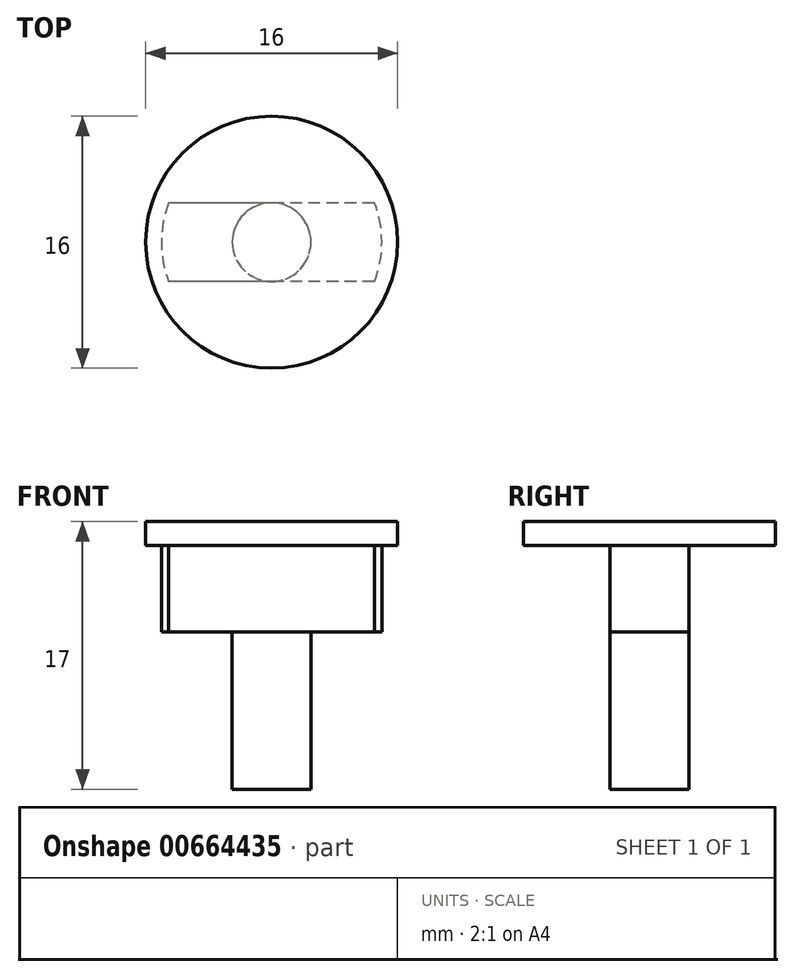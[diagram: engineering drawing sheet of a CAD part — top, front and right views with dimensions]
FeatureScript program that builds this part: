
annotation { "Feature Type Name" : "Feature", "Feature Type Description" : "" }
export const myFeature = defineFeature(function(context is Context, id is Id, definition is map)
    precondition{}
    {
        {
            var Q0;
            Q0=qCreatedBy(makeId("Front.planeOp"),FACE);
            var sketch = newSketch(context, id + "F0", { "sketchPlane" : qUnion([Q0])});
            skLineSegment(sketch, "E0", {"start": v(24.56, 9.47) * mm, "end": v(24.56, 26.47) * mm});
            skLineSegment(sketch, "E1", {"start": v(24.56, 26.47) * mm, "end": v(32.56, 26.47) * mm});
            skLineSegment(sketch, "E2", {"start": v(32.56, 26.47) * mm, "end": v(32.56, 24.97) * mm});
            skLineSegment(sketch, "E3", {"start": v(32.56, 24.97) * mm, "end": v(31.56, 24.97) * mm});
            skLineSegment(sketch, "E4", {"start": v(31.56, 24.97) * mm, "end": v(31.56, 19.47) * mm});
            skLineSegment(sketch, "E5", {"start": v(31.56, 19.47) * mm, "end": v(27.06, 19.47) * mm});
            skLineSegment(sketch, "E6", {"start": v(27.06, 19.47) * mm, "end": v(27.06, 9.47) * mm});
            skLineSegment(sketch, "E7", {"start": v(27.06, 9.47) * mm, "end": v(24.56, 9.47) * mm});
            skSolve(sketch);
        }
        {
            var Q0;
            Q0=makeQuery(id+"F0.imprint","IMPRINT",FACE,{"disambiguationData":[TD([[makeQuery(id+"F0.imprint","IMPRINT",EDGE,{"derivedFrom":sQuery(id+"F0.wireOp",EDGE,"E0")}),-1.0]])]});
            var Q1;
            Q1=sQuery(id+"F0.wireOp",EDGE,"E0");
            revolve(context, id + "F1", {"surfaceOperationType" : NewSurfaceOperationType.NEW, "entities" : qUnion([Q0]), "axis" : qUnion([Q1]), "revolveType" : RevolveType.FULL});
        }
        {
            var Q0;
            Q0=makeQuery(id+"F1.opRevolve","SWEPT_FACE",FACE,{"disambiguationData":[OSD([sQuery(id+"F0.wireOp",EDGE,"E5")])]});
            var sketch = newSketch(context, id + "F2", { "sketchPlane" : qUnion([Q0])});
            skLineSegment(sketch, "E8", {"start": v(24.56, 0) * mm, "end": v(33.86, 0) * mm});
            skCircle(sketch, "E9.0", {"center": v(24.56, 0) * mm, "radius": 2.5 * mm});
            skLineSegment(sketch, "E10.bottom", {"start": v(33.81, 7.34) * mm, "end": v(14.98, 7.34) * mm});
            skLineSegment(sketch, "E10.top", {"start": v(33.81, 2.5) * mm, "end": v(14.98, 2.5) * mm});
            skLineSegment(sketch, "E10.left", {"start": v(33.81, 7.34) * mm, "end": v(33.81, 2.5) * mm});
            skLineSegment(sketch, "E10.right", {"start": v(14.98, 7.34) * mm, "end": v(14.98, 2.5) * mm});
            skLineSegment(sketch, "E11.MirrorCS", {"start": v(33.81, -2.5) * mm, "end": v(14.98, -2.5) * mm});
            skLineSegment(sketch, "E12.MirrorCS", {"start": v(14.98, -7.34) * mm, "end": v(14.98, -2.5) * mm});
            skLineSegment(sketch, "E13.MirrorCS", {"start": v(33.81, -7.34) * mm, "end": v(14.98, -7.34) * mm});
            skLineSegment(sketch, "E14.MirrorCS", {"start": v(33.81, -7.34) * mm, "end": v(33.81, -2.5) * mm});
            skSolve(sketch);
        }
        {
            var Q0;
            {var subQ0=sQuery(id+"F2.wireOp",EDGE,"E10.top");var subQ1=makeQuery(id+"F2.imprint","INTERSECT",VERTEX,{"derivedFrom":[sQuery(id+"F2.wireOp",EDGE,"E9.0"),subQ0]});Q0=makeQuery(id+"F2.imprint","IMPRINT",FACE,{"disambiguationData":[TD([[makeQuery(id+"F2.imprint","IMPRINT",EDGE,{"disambiguationData":[TD([[subQ1,1.0]])],"derivedFrom":subQ0}),-1.0]])]});}
            var Q1;
            {var subQ0=sQuery(id+"F2.wireOp",EDGE,"E11.MirrorCS");var subQ1=makeQuery(id+"F2.imprint","INTERSECT",VERTEX,{"derivedFrom":[sQuery(id+"F2.wireOp",EDGE,"E9.0"),subQ0]});Q1=makeQuery(id+"F2.imprint","IMPRINT",FACE,{"disambiguationData":[TD([[makeQuery(id+"F2.imprint","IMPRINT",EDGE,{"disambiguationData":[TD([[subQ1,1.0]])],"derivedFrom":subQ0}),1.0]])]});}
            var Q2;
            Q2=makeQuery(id+"F1.opRevolve","SWEPT_FACE",FACE,{"disambiguationData":[OSD([sQuery(id+"F0.wireOp",EDGE,"E3")])]});
            extrude(context, id + "F3", {"entities" : qUnion([Q0, Q1]), "operationType" : NewBodyOperationType.REMOVE, "endBound" : BoundingType.UP_TO_SURFACE, "oppositeDirection" : true, "depth" : 25 * mm, "endBoundEntityFace" : qUnion([Q2]), "offsetDistance" : 25 * mm});
        }
    });
